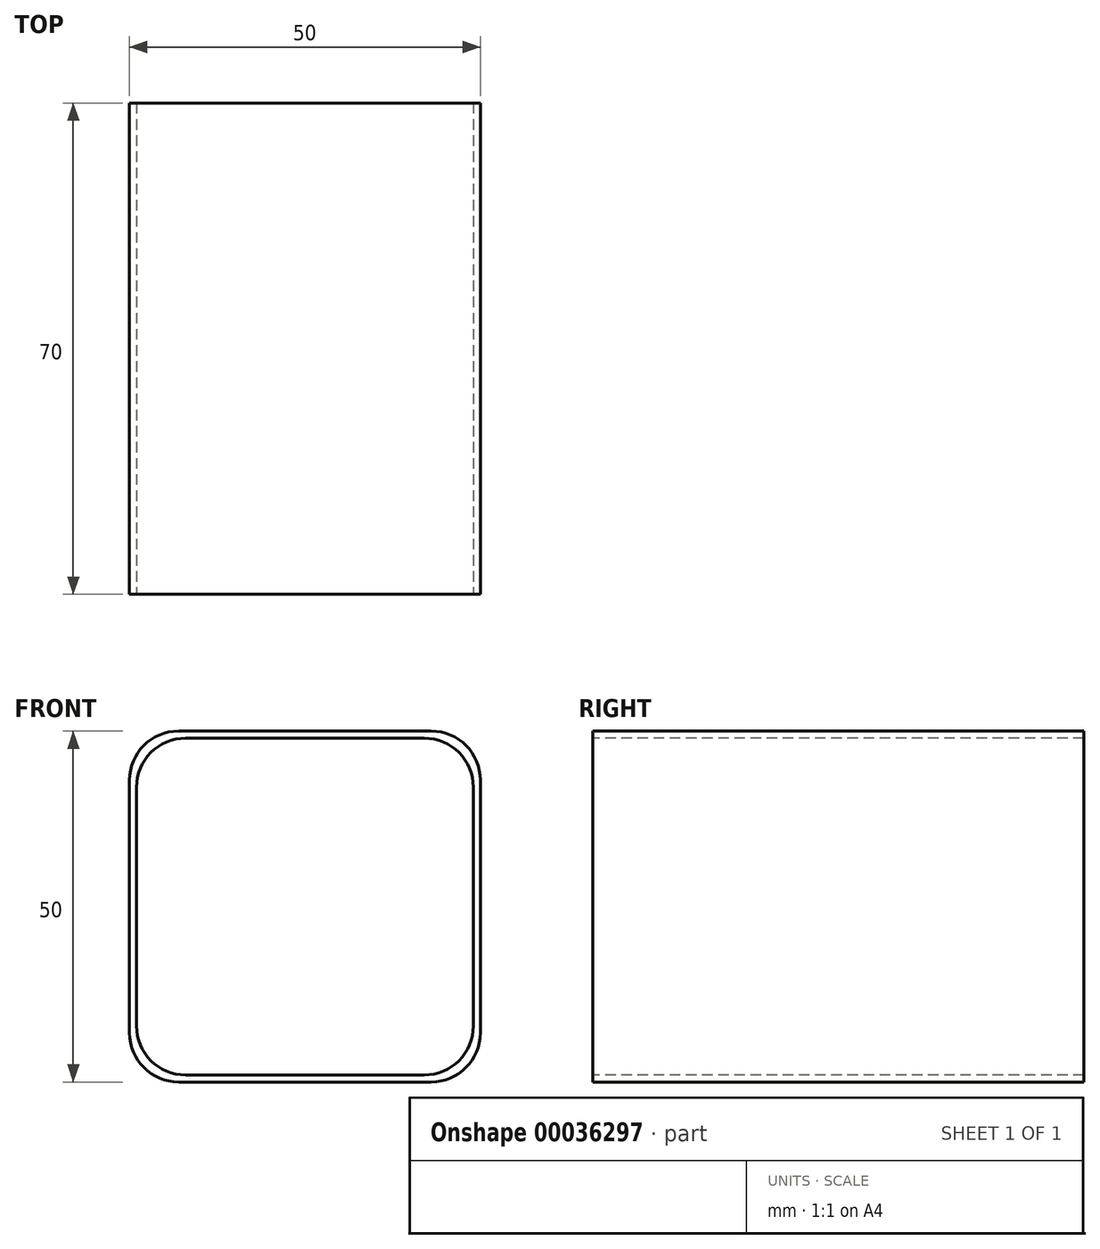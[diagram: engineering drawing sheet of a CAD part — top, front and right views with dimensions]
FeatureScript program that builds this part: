
annotation { "Feature Type Name" : "Feature", "Feature Type Description" : "" }
export const myFeature = defineFeature(function(context is Context, id is Id, definition is map)
    precondition{}
    {
        {
            var Q0;
            Q0=qCreatedBy(makeId("Top.planeOp"),FACE);
            var sketch = newSketch(context, id + "F0", { "sketchPlane" : qUnion([Q0])});
            skLineSegment(sketch, "E0.bottom", {"start": v(7, 0) * mm, "end": v(43, 0) * mm});
            skLineSegment(sketch, "E0.top", {"start": v(7, -50) * mm, "end": v(43, -50) * mm});
            skLineSegment(sketch, "E0.left", {"start": v(0, -7) * mm, "end": v(0, -43) * mm});
            skLineSegment(sketch, "E0.right", {"start": v(50, -7) * mm, "end": v(50, -43) * mm});
            skLineSegment(sketch, "E1.0", {"start": v(8, -1) * mm, "end": v(42, -1) * mm});
            skLineSegment(sketch, "E1.1", {"start": v(1, -8) * mm, "end": v(1, -42) * mm});
            skLineSegment(sketch, "E1.2", {"start": v(8, -49) * mm, "end": v(42, -49) * mm});
            skLineSegment(sketch, "E1.3", {"start": v(49, -8) * mm, "end": v(49, -42) * mm});
            skPoint(sketch, "E2.visualSharp", {"position": v(0, 0) * mm});
            skArc(sketch, "E2.filletArc", {"start": v(7, 0) * mm, "mid": v(2.05, -2.05) * mm, "end": v(0, -7) * mm});
            skPoint(sketch, "E3.visualSharp", {"position": v(1, -1) * mm});
            skArc(sketch, "E3.filletArc", {"start": v(8, -1) * mm, "mid": v(3.05, -3.05) * mm, "end": v(1, -8) * mm});
            skPoint(sketch, "E4.visualSharp", {"position": v(1, -49) * mm});
            skArc(sketch, "E4.filletArc", {"start": v(1, -42) * mm, "mid": v(3.05, -46.95) * mm, "end": v(8, -49) * mm});
            skPoint(sketch, "E5.visualSharp", {"position": v(0, -50) * mm});
            skArc(sketch, "E5.filletArc", {"start": v(0, -43) * mm, "mid": v(2.05, -47.95) * mm, "end": v(7, -50) * mm});
            skPoint(sketch, "E6.visualSharp", {"position": v(49, -49) * mm});
            skArc(sketch, "E6.filletArc", {"start": v(42, -49) * mm, "mid": v(46.95, -46.95) * mm, "end": v(49, -42) * mm});
            skPoint(sketch, "E7.visualSharp", {"position": v(50, -50) * mm});
            skArc(sketch, "E7.filletArc", {"start": v(43, -50) * mm, "mid": v(47.95, -47.95) * mm, "end": v(50, -43) * mm});
            skPoint(sketch, "E8.visualSharp", {"position": v(49, -1) * mm});
            skArc(sketch, "E8.filletArc", {"start": v(49, -8) * mm, "mid": v(46.95, -3.05) * mm, "end": v(42, -1) * mm});
            skPoint(sketch, "E9.visualSharp", {"position": v(50, 0) * mm});
            skArc(sketch, "E9.filletArc", {"start": v(50, -7) * mm, "mid": v(47.95, -2.05) * mm, "end": v(43, 0) * mm});
            skSolve(sketch);
        }
        {
            var Q0;
            Q0=qSketchRegion(id+"F0",true);
            extrude(context, id + "F1", {"entities" : qUnion([Q0]), "oppositeDirection" : true, "depth" : 70 * mm});
        }
        {
            var Q0;
            Q0=makeQuery(id+"F1.opExtrude","SWEPT_BODY",BODY,{"disambiguationData":[OSD([sQuery(id+"F0.wireOp",EDGE,"E0.bottom"),sQuery(id+"F0.wireOp",EDGE,"E0.top"),sQuery(id+"F0.wireOp",EDGE,"E0.left"),sQuery(id+"F0.wireOp",EDGE,"E0.right"),sQuery(id+"F0.wireOp",EDGE,"E1.0"),sQuery(id+"F0.wireOp",EDGE,"E1.1"),sQuery(id+"F0.wireOp",EDGE,"E1.2"),sQuery(id+"F0.wireOp",EDGE,"E1.3"),sQuery(id+"F0.wireOp",EDGE,"E2.filletArc"),sQuery(id+"F0.wireOp",EDGE,"E3.filletArc"),sQuery(id+"F0.wireOp",EDGE,"E4.filletArc"),sQuery(id+"F0.wireOp",EDGE,"E5.filletArc"),sQuery(id+"F0.wireOp",EDGE,"E6.filletArc"),sQuery(id+"F0.wireOp",EDGE,"E7.filletArc"),sQuery(id+"F0.wireOp",EDGE,"E8.filletArc"),sQuery(id+"F0.wireOp",EDGE,"E9.filletArc")])]});
            var Q1;
            Q1=makeQuery(id+"F1.opExtrude","CAP_EDGE",EDGE,{"disambiguationData":[OSD([sQuery(id+"F0.wireOp",EDGE,"E0.bottom")])],"isStart":true});
            transform(context, id + "F2", {"entities" : qUnion([Q0]), "transformType" : TransformType.ROTATION, "transformAxis" : qUnion([Q1]), "angle" : 90 * degree, "makeCopy" : false});
        }
    });
